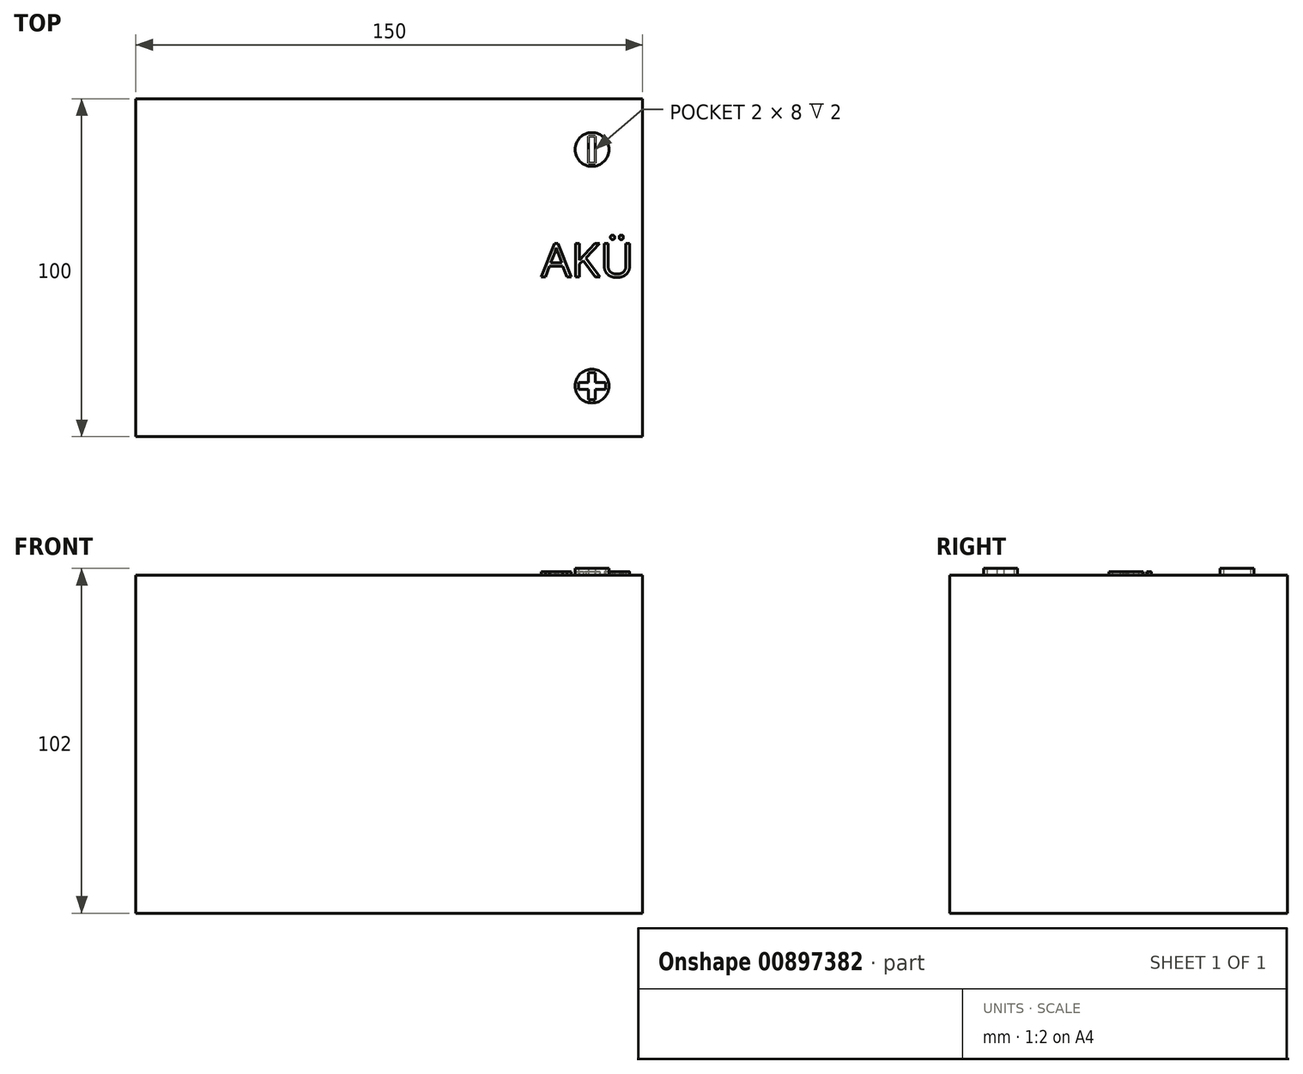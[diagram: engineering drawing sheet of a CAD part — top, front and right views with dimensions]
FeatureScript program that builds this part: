
annotation { "Feature Type Name" : "Feature", "Feature Type Description" : "" }
export const myFeature = defineFeature(function(context is Context, id is Id, definition is map)
    precondition{}
    {
        {
            var Q0;
            Q0=qCreatedBy(makeId("Top.planeOp"),FACE);
            var sketch = newSketch(context, id + "F0", { "sketchPlane" : qUnion([Q0])});
            skLineSegment(sketch, "E0.bottom", {"start": v(0, 0) * mm, "end": v(-150, 0) * mm});
            skLineSegment(sketch, "E0.top", {"start": v(0, 100) * mm, "end": v(-150, 100) * mm});
            skLineSegment(sketch, "E0.left", {"start": v(0, 0) * mm, "end": v(0, 100) * mm});
            skLineSegment(sketch, "E0.right", {"start": v(-150, 0) * mm, "end": v(-150, 100) * mm});
            skSolve(sketch);
        }
        {
            var Q0;
            Q0 = qSketchRegion(id + "F0", true);
            extrude(context, id + "F1", {"entities" : qUnion([Q0]), "depth" : 100 * mm, "offsetDistance" : 25 * mm});
        }
        {
            var Q0;
            Q0=makeQuery(id+"F1.opExtrude","CAP_FACE",FACE,{"disambiguationData":[OSD([sQuery(id+"F0.wireOp",EDGE,"E0.bottom"),sQuery(id+"F0.wireOp",EDGE,"E0.top"),sQuery(id+"F0.wireOp",EDGE,"E0.left"),sQuery(id+"F0.wireOp",EDGE,"E0.right")])],"isStart":false});
            var sketch = newSketch(context, id + "F2", { "sketchPlane" : qUnion([Q0])});
            skCircle(sketch, "E1", {"center": v(-15, 15) * mm, "radius": 5 * mm});
            skCircle(sketch, "E2", {"center": v(-15, 85) * mm, "radius": 5 * mm});
            skLineSegment(sketch, "E3.bottom", {"start": v(-16, 89) * mm, "end": v(-14, 89) * mm});
            skLineSegment(sketch, "E3.top", {"start": v(-16, 81) * mm, "end": v(-14, 81) * mm});
            skLineSegment(sketch, "E3.left", {"start": v(-16, 89) * mm, "end": v(-16, 81) * mm});
            skLineSegment(sketch, "E3.right", {"start": v(-14, 89) * mm, "end": v(-14, 81) * mm});
            skLineSegment(sketch, "E4.bottom", {"start": v(-16, 19) * mm, "end": v(-14, 19) * mm});
            skLineSegment(sketch, "E4.top", {"start": v(-16, 11) * mm, "end": v(-14, 11) * mm});
            skLineSegment(sketch, "E4.left", {"start": v(-16, 19) * mm, "end": v(-16, 16) * mm});
            skLineSegment(sketch, "E4.right", {"start": v(-14, 19) * mm, "end": v(-14, 16) * mm});
            skLineSegment(sketch, "E5.bottom", {"start": v(-19, 16) * mm, "end": v(-16, 16) * mm});
            skLineSegment(sketch, "E5.top", {"start": v(-19, 14) * mm, "end": v(-16, 14) * mm});
            skLineSegment(sketch, "E5.left", {"start": v(-19, 16) * mm, "end": v(-19, 14) * mm});
            skLineSegment(sketch, "E5.right", {"start": v(-11, 16) * mm, "end": v(-11, 14) * mm});
            skLineSegment(sketch, "E6.trimOffspring", {"start": v(-16, 14) * mm, "end": v(-16, 11) * mm});
            skLineSegment(sketch, "E7.trimOffspring", {"start": v(-14, 16) * mm, "end": v(-11, 16) * mm});
            skLineSegment(sketch, "E8.trimOffspring", {"start": v(-14, 14) * mm, "end": v(-14, 11) * mm});
            skLineSegment(sketch, "E9.trimOffspring", {"start": v(-14, 14) * mm, "end": v(-11, 14) * mm});
            skText(sketch, "E10", { "text": "AKÜ", "fontName": "OpenSans-Regular.ttf"});
            const initialGuessF2  = {"E10": [-0.02998, 0.04727, 1, 0, 0.01]};
            skSetInitialGuess(sketch, initialGuessF2);
            skSolve(sketch);
        }
        {
            var Q0;
            Q0=makeQuery(id+"F2.imprint","IMPRINT",FACE,{"disambiguationData":[TD([[makeQuery(id+"F2.imprint","IMPRINT",EDGE,{"derivedFrom":sQuery(id+"F2.wireOp",EDGE,"E1")}),1.0]])]});
            var Q1;
            Q1=makeQuery(id+"F2.imprint","IMPRINT",FACE,{"disambiguationData":[TD([[makeQuery(id+"F2.imprint","IMPRINT",EDGE,{"derivedFrom":sQuery(id+"F2.wireOp",EDGE,"E2")}),1.0]])]});
            extrude(context, id + "F3", {"entities" : qUnion([Q0, Q1]), "operationType" : NewBodyOperationType.ADD, "depth" : 2 * mm, "offsetDistance" : 25 * mm});
        }
        {
            var Q0;
            Q0 = qSketchRegion(id + "F2", true);
            extrude(context, id + "F4", {"entities" : qUnion([Q0]), "operationType" : NewBodyOperationType.ADD, "depth" : 1 * mm, "offsetDistance" : 25 * mm});
        }
    });
